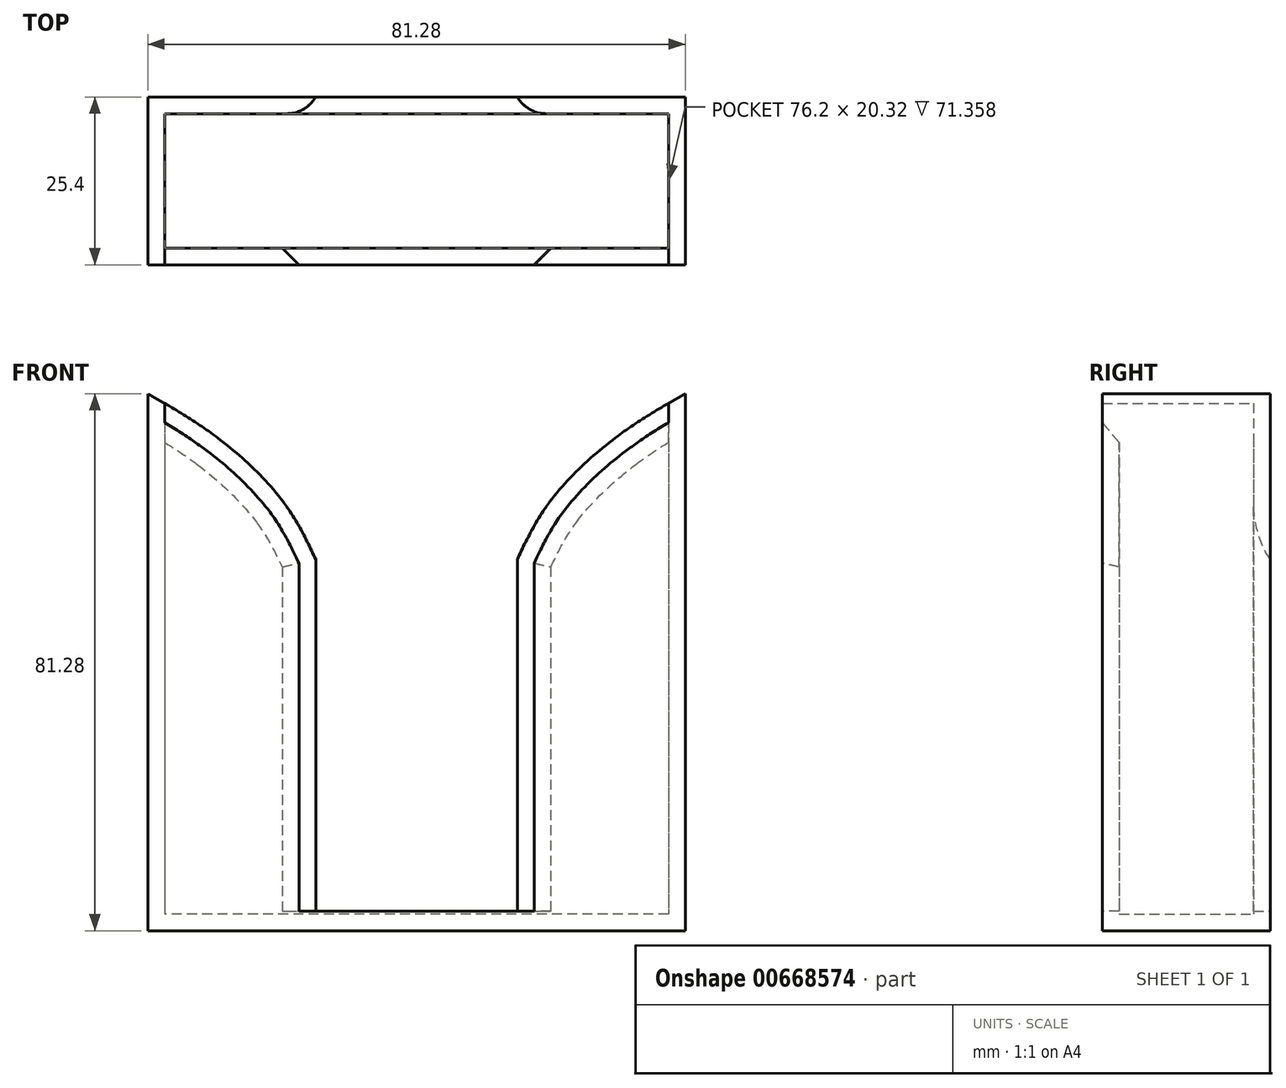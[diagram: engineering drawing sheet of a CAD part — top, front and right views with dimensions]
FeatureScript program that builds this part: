
annotation { "Feature Type Name" : "Feature", "Feature Type Description" : "" }
export const myFeature = defineFeature(function(context is Context, id is Id, definition is map)
    precondition{}
    {
        {
            var Q0;
            Q0=qCreatedBy(makeId("Front.planeOp"),FACE);
            var sketch = newSketch(context, id + "F0", { "sketchPlane" : qUnion([Q0])});
            skLineSegment(sketch, "E0.bottom", {"start": v(40.64, 40.64) * mm, "end": v(-40.64, 40.64) * mm});
            skLineSegment(sketch, "E0.top", {"start": v(40.64, -40.64) * mm, "end": v(-40.64, -40.64) * mm});
            skLineSegment(sketch, "E0.left", {"start": v(40.64, 40.64) * mm, "end": v(40.64, -40.64) * mm});
            skLineSegment(sketch, "E0.right", {"start": v(-40.64, 40.64) * mm, "end": v(-40.64, -40.64) * mm});
            skPoint(sketch, "E0.middle", {"position": v(0, 0) * mm});
            skLineSegment(sketch, "E1.bottom", {"start": v(40.64, -40.64) * mm, "end": v(71.12, -40.64) * mm});
            skLineSegment(sketch, "E1.top", {"start": v(40.64, -10.16) * mm, "end": v(71.12, -10.16) * mm});
            skLineSegment(sketch, "E1.left", {"start": v(40.64, -40.64) * mm, "end": v(40.64, -10.16) * mm});
            skLineSegment(sketch, "E1.right", {"start": v(71.12, -40.64) * mm, "end": v(71.12, -10.16) * mm});
            skLineSegment(sketch, "E2.bottom", {"start": v(-30.08, 33.96) * mm, "end": v(30.08, 33.96) * mm});
            skLineSegment(sketch, "E2.top", {"start": v(-30.08, -33.96) * mm, "end": v(30.08, -33.96) * mm});
            skLineSegment(sketch, "E2.left", {"start": v(-30.08, 33.96) * mm, "end": v(-30.08, -33.96) * mm});
            skLineSegment(sketch, "E2.right", {"start": v(30.08, 33.96) * mm, "end": v(30.08, -33.96) * mm});
            skLineSegment(sketch, "E3.bottom", {"start": v(-20.12, 24.22) * mm, "end": v(20.12, 24.22) * mm});
            skLineSegment(sketch, "E3.top", {"start": v(-20.12, -24.22) * mm, "end": v(20.12, -24.22) * mm});
            skLineSegment(sketch, "E3.left", {"start": v(-20.12, 24.22) * mm, "end": v(-20.12, -24.22) * mm});
            skLineSegment(sketch, "E3.right", {"start": v(20.12, 24.22) * mm, "end": v(20.12, -24.22) * mm});
            skLineSegment(sketch, "E4.bottom", {"start": v(-15.24, 15.55) * mm, "end": v(15.24, 15.55) * mm});
            skLineSegment(sketch, "E4.top", {"start": v(-15.24, -15.55) * mm, "end": v(15.24, -15.55) * mm});
            skLineSegment(sketch, "E4.left", {"start": v(-15.24, 15.55) * mm, "end": v(-15.24, -15.55) * mm});
            skLineSegment(sketch, "E4.right", {"start": v(15.24, 15.55) * mm, "end": v(15.24, -15.55) * mm});
            skFitSpline(sketch, "E5", {"points": [v(-40.64, 40.64) * mm, v(-30.08, 33.96) * mm, v(-20.12, 24.22) * mm, v(-15.24, 15.55) * mm], "startDerivative": vector(31.17, -17.85) * mm, "endDerivative": vector(13.45, -28.54) * mm});
            skFitSpline(sketch, "E6", {"points": [v(40.64, 40.64) * mm, v(30.08, 33.96) * mm, v(20.12, 24.22) * mm, v(15.24, 15.55) * mm], "startDerivative": vector(-31.17, -17.85) * mm, "endDerivative": vector(-13.45, -28.54) * mm});
            skLineSegment(sketch, "E7", {"start": v(-15.24, -15.55) * mm, "end": v(-15.24, -40.64) * mm});
            skLineSegment(sketch, "E8", {"start": v(-15.24, -40.64) * mm, "end": v(-15.24, -15.55) * mm});
            skLineSegment(sketch, "E9", {"start": v(15.24, -15.55) * mm, "end": v(15.24, -40.64) * mm});
            skLineSegment(sketch, "E10", {"start": v(-40.64, -37.69) * mm, "end": v(40.64, -37.69) * mm});
            skSolve(sketch);
        }
        {
            var Q0;
            {var subQ3=sQuery(id+"F0.wireOp",EDGE,"E2.left");Q0=makeQuery(id+"F0.imprint","IMPRINT",FACE,{"disambiguationData":[TD([[makeQuery(id+"F0.imprint","IMPRINT",EDGE,{"derivedFrom":subQ3}),-1.0]])]});}
            var Q1;
            {var subQ0=sQuery(id+"F0.wireOp",EDGE,"E0.right");var subQ1=sQuery(id+"F0.wireOp",EDGE,"E0.top");var subQ2=makeQuery(id+"F0.imprint","INTERSECT",VERTEX,{"derivedFrom":[subQ1,subQ0]});Q1=makeQuery(id+"F0.imprint","IMPRINT",FACE,{"disambiguationData":[TD([[makeQuery(id+"F0.imprint","IMPRINT",EDGE,{"disambiguationData":[TD([[subQ2,1.0]])],"derivedFrom":subQ1}),-1.0]])]});}
            var Q2;
            {var subQ4=sQuery(id+"F0.wireOp",EDGE,"E2.left");Q2=makeQuery(id+"F0.imprint","IMPRINT",FACE,{"disambiguationData":[TD([[makeQuery(id+"F0.imprint","IMPRINT",EDGE,{"derivedFrom":subQ4}),1.0]])]});}
            var Q3;
            {var subQ0=sQuery(id+"F0.wireOp",EDGE,"E8");var subQ1=sQuery(id+"F0.wireOp",EDGE,"E0.top");var subQ2=makeQuery(id+"F0.imprint","INTERSECT",VERTEX,{"derivedFrom":[subQ1,subQ0]});Q3=makeQuery(id+"F0.imprint","IMPRINT",FACE,{"disambiguationData":[TD([[makeQuery(id+"F0.imprint","IMPRINT",EDGE,{"disambiguationData":[TD([[subQ2,1.0]])],"derivedFrom":subQ1}),-1.0]])]});}
            var Q4;
            {var subQ1=sQuery(id+"F0.wireOp",EDGE,"E0.top");var subQ3=sQuery(id+"F0.wireOp",EDGE,"E9");var subQ4=makeQuery(id+"F0.imprint","INTERSECT",VERTEX,{"derivedFrom":[subQ1,subQ3]});Q4=makeQuery(id+"F0.imprint","IMPRINT",FACE,{"disambiguationData":[TD([[makeQuery(id+"F0.imprint","IMPRINT",EDGE,{"disambiguationData":[TD([[subQ4,1.0]])],"derivedFrom":subQ3}),1.0]])]});}
            var Q5;
            {var subQ4=sQuery(id+"F0.wireOp",EDGE,"E0.left");Q5=makeQuery(id+"F0.imprint","IMPRINT",FACE,{"disambiguationData":[TD([[makeQuery(id+"F0.imprint","IMPRINT",EDGE,{"derivedFrom":subQ4}),-1.0]])]});}
            var Q6;
            {var subQ4=sQuery(id+"F0.wireOp",EDGE,"E2.right");Q6=makeQuery(id+"F0.imprint","IMPRINT",FACE,{"disambiguationData":[TD([[makeQuery(id+"F0.imprint","IMPRINT",EDGE,{"derivedFrom":subQ4}),-1.0]])]});}
            var Q7;
            {var subQ1=sQuery(id+"F0.wireOp",EDGE,"E3.right");Q7=makeQuery(id+"F0.imprint","IMPRINT",FACE,{"disambiguationData":[TD([[makeQuery(id+"F0.imprint","IMPRINT",EDGE,{"derivedFrom":subQ1}),-1.0]])]});}
            var Q8;
            {var subQ1=sQuery(id+"F0.wireOp",EDGE,"E3.left");Q8=makeQuery(id+"F0.imprint","IMPRINT",FACE,{"disambiguationData":[TD([[makeQuery(id+"F0.imprint","IMPRINT",EDGE,{"derivedFrom":subQ1}),1.0]])]});}
            extrude(context, id + "F1", {"entities" : qUnion([Q0, Q1, Q2, Q3, Q4, Q5, Q6, Q7, Q8]), "depth" : 25.4 * mm, "offsetDistance" : 25.4 * mm});
        }
        {
            var Q0;
            Q0=makeQuery(id+"F1.opExtrude","SWEPT_FACE",FACE,{"disambiguationData":[OSD([sQuery(id+"F0.wireOp",EDGE,"E5")])]});
            var Q1;
            Q1=makeQuery(id+"F1.opExtrude","SWEPT_FACE",FACE,{"disambiguationData":[OSD([sQuery(id+"F0.wireOp",EDGE,"E4.left"),sQuery(id+"F0.wireOp",EDGE,"E8")])]});
            var Q2;
            Q2=makeQuery(id+"F1.opExtrude","SWEPT_FACE",FACE,{"disambiguationData":[OSD([sQuery(id+"F0.wireOp",EDGE,"E10")])]});
            var Q3;
            Q3=makeQuery(id+"F1.opExtrude","SWEPT_FACE",FACE,{"disambiguationData":[OSD([sQuery(id+"F0.wireOp",EDGE,"E4.right"),sQuery(id+"F0.wireOp",EDGE,"E9")])]});
            var Q4;
            Q4=makeQuery(id+"F1.opExtrude","SWEPT_FACE",FACE,{"disambiguationData":[OSD([sQuery(id+"F0.wireOp",EDGE,"E6")])]});
            shell(context, id + "F2", {"entities" : qUnion([Q0, Q1, Q2, Q3, Q4]), "thickness" : 2.54 * mm});
        }
        {
            var Q0;
            {var subQ0=sQuery(id+"F0.wireOp",EDGE,"E6");Q0=makeQuery(id+"F2.opShell","OFFSET_EDGE",EDGE,{"disambiguationData":[OSD([subQ0]),TDD([makeQuery(id+"F1.opExtrude","CAP_EDGE",EDGE,{"disambiguationData":[OSD([subQ0])],"isStart":false})])]});}
            var Q1;
            {var subQ0=sQuery(id+"F0.wireOp",EDGE,"E9");var subQ1=sQuery(id+"F0.wireOp",EDGE,"E4.right");Q1=makeQuery(id+"F2.opShell","OFFSET_EDGE",EDGE,{"disambiguationData":[OSD([subQ1,subQ0]),TDD([makeQuery(id+"F1.opExtrude","CAP_EDGE",EDGE,{"disambiguationData":[OSD([subQ1,subQ0])],"isStart":false})])]});}
            var Q2;
            {var subQ0=sQuery(id+"F0.wireOp",EDGE,"E5");Q2=makeQuery(id+"F2.opShell","OFFSET_EDGE",EDGE,{"disambiguationData":[OSD([subQ0]),TDD([makeQuery(id+"F1.opExtrude","CAP_EDGE",EDGE,{"disambiguationData":[OSD([subQ0])],"isStart":false})])]});}
            var Q3;
            {var subQ0=sQuery(id+"F0.wireOp",EDGE,"E8");var subQ1=sQuery(id+"F0.wireOp",EDGE,"E4.left");Q3=makeQuery(id+"F2.opShell","OFFSET_EDGE",EDGE,{"disambiguationData":[OSD([subQ1,subQ0]),TDD([makeQuery(id+"F1.opExtrude","CAP_EDGE",EDGE,{"disambiguationData":[OSD([subQ1,subQ0])],"isStart":false})])]});}
            chamfer(context, id + "F3", {"entities" : qUnion([Q0, Q1, Q2, Q3]), "width" : 5.08 * mm, "tangentPropagation" : true});
        }
        {
            var Q0;
            {var subQ0=sQuery(id+"F0.wireOp",EDGE,"E8");var subQ1=sQuery(id+"F0.wireOp",EDGE,"E4.left");Q0=makeQuery(id+"F2.opShell","OFFSET_EDGE",EDGE,{"disambiguationData":[OSD([subQ1,subQ0]),TDD([makeQuery(id+"F1.opExtrude","CAP_EDGE",EDGE,{"disambiguationData":[OSD([subQ1,subQ0])],"isStart":true})])]});}
            var Q1;
            {var subQ0=sQuery(id+"F0.wireOp",EDGE,"E9");var subQ1=sQuery(id+"F0.wireOp",EDGE,"E4.right");Q1=makeQuery(id+"F2.opShell","OFFSET_EDGE",EDGE,{"disambiguationData":[OSD([subQ1,subQ0]),TDD([makeQuery(id+"F1.opExtrude","CAP_EDGE",EDGE,{"disambiguationData":[OSD([subQ1,subQ0])],"isStart":true})])]});}
            fillet(context, id + "F4", {"entities" : qUnion([Q0, Q1]), "radius" : 5.08 * mm, "tangentPropagation" : true, "allowEdgeOverflow" : false});
        }
    });
